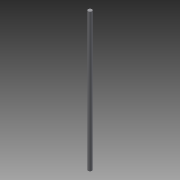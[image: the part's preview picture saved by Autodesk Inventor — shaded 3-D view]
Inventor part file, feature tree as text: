
AUTODESK INVENTOR PART (.ipt)
format: ipt  version: 2013 (Build 170138000, 138)  size: 61,440 bytes
history: native  units: in
note: dims shown in document units (in); Inventor stores cm internally (conversion verified against a paired STEP export)
features: extrude x1, sketch x1
ambient origin geometry x8: Origin, YZ Plane, XZ Plane, XY Plane, X Axis, Y Axis, Z Axis, Center Point
bodies: Solid1 (feature_tree)
feature tree (2):
  extrude  "Extrusion1"  Depth=18.0in TaperAngle=0.0deg
  sketch  "Sketch1"  dims[d0=0.5in d1=18.0in d2=0.0in]
